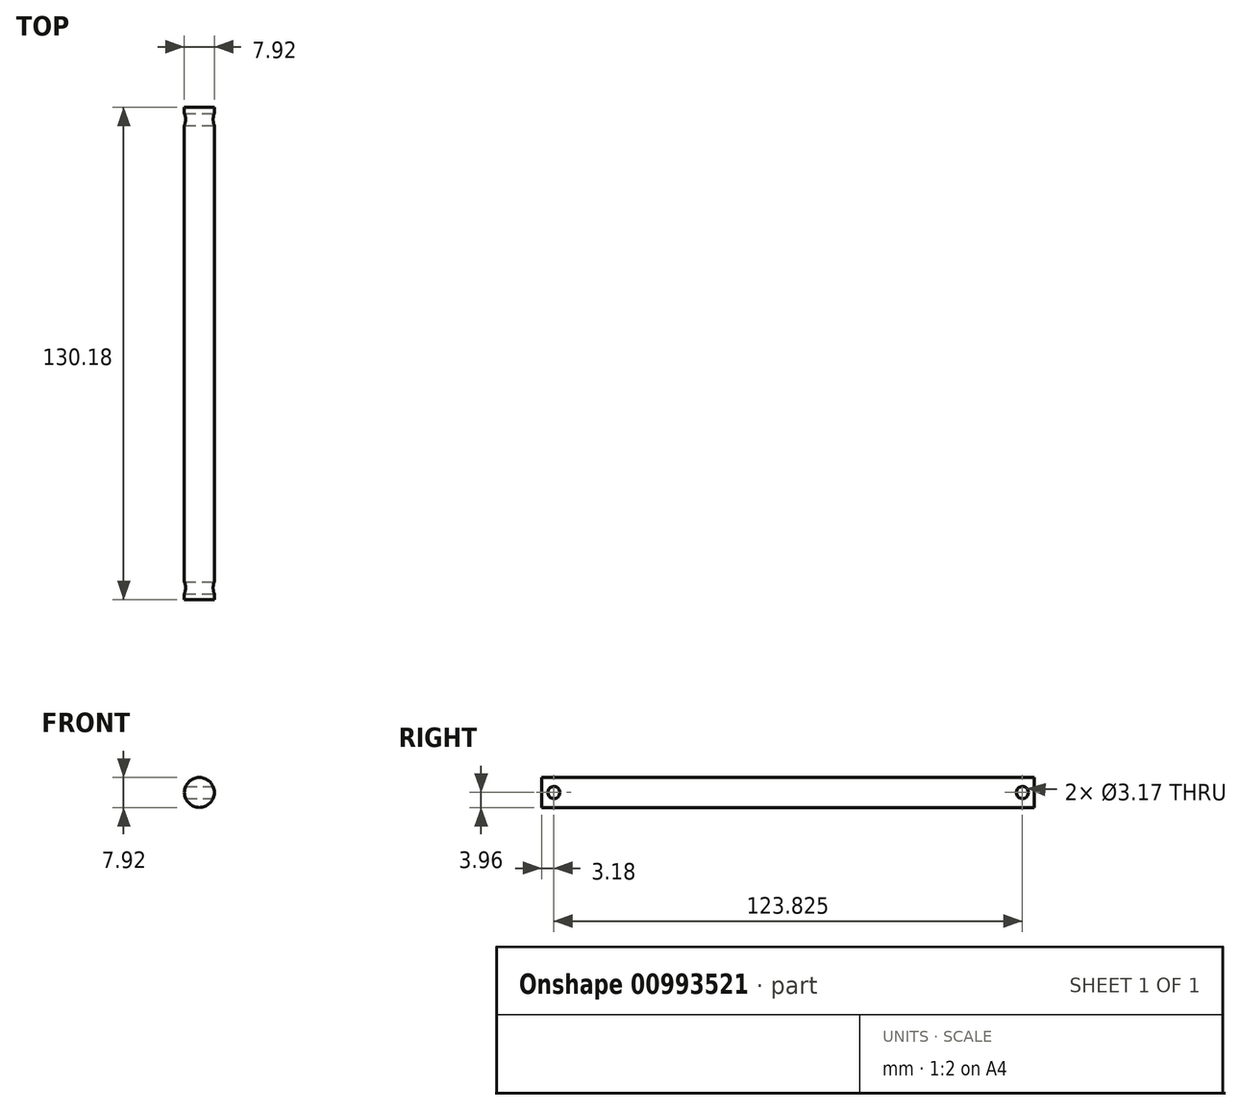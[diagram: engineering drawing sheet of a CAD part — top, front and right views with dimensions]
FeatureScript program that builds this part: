
annotation { "Feature Type Name" : "Feature", "Feature Type Description" : "" }
export const myFeature = defineFeature(function(context is Context, id is Id, definition is map)
    precondition{}
    {
        {
            var Q0;
            Q0=qCreatedBy(makeId("Front.planeOp"),FACE);
            var sketch = newSketch(context, id + "F0", { "sketchPlane" : qUnion([Q0])});
            skLineSegment(sketch, "E0.bottom", {"start": v(3.96, -3.96) * mm, "end": v(-3.96, -3.96) * mm});
            skLineSegment(sketch, "E0.top", {"start": v(3.96, 3.96) * mm, "end": v(-3.96, 3.96) * mm});
            skLineSegment(sketch, "E0.left", {"start": v(3.96, -3.96) * mm, "end": v(3.96, 3.96) * mm});
            skLineSegment(sketch, "E0.right", {"start": v(-3.96, -3.96) * mm, "end": v(-3.96, 3.96) * mm});
            skPoint(sketch, "E0.middle", {"position": v(0, 0) * mm});
            skSolve(sketch);
        }
        {
            var Q0;
            Q0=makeQuery(id+"F0.imprint","IMPRINT",FACE,{"disambiguationData":[TD([[makeQuery(id+"F0.imprint","IMPRINT",EDGE,{"derivedFrom":sQuery(id+"F0.wireOp",EDGE,"E0.bottom")}),-1.0]])]});
            extrude(context, id + "F1", {"entities" : qUnion([Q0]), "depth" : 130.17 * mm, "offsetDistance" : 25.4 * mm});
        }
        {
            var Q0;
            Q0=makeQuery(id+"F1.opExtrude","SWEPT_FACE",FACE,{"disambiguationData":[OSD([sQuery(id+"F0.wireOp",EDGE,"E0.left")])]});
            var sketch = newSketch(context, id + "F2", { "sketchPlane" : qUnion([Q0])});
            skLineSegment(sketch, "E1", {"start": v(0, 0) * mm, "end": v(-3.18, 0) * mm});
            skCircle(sketch, "E2", {"center": v(-3.18, 0) * mm, "radius": 1.59 * mm});
            skLineSegment(sketch, "E3", {"start": v(-130.18, 0) * mm, "end": v(-127, 0) * mm});
            skCircle(sketch, "E4", {"center": v(-127, 0) * mm, "radius": 1.59 * mm});
            skSolve(sketch);
        }
        {
            var Q0;
            Q0=makeQuery(id+"F2.imprint","IMPRINT",FACE,{"disambiguationData":[TD([[makeQuery(id+"F2.imprint","IMPRINT",EDGE,{"derivedFrom":sQuery(id+"F2.wireOp",EDGE,"E4")}),1.0]])]});
            var Q1;
            Q1=makeQuery(id+"F2.imprint","IMPRINT",FACE,{"disambiguationData":[TD([[makeQuery(id+"F2.imprint","IMPRINT",EDGE,{"derivedFrom":sQuery(id+"F2.wireOp",EDGE,"E2")}),1.0]])]});
            extrude(context, id + "F3", {"entities" : qUnion([Q0, Q1]), "operationType" : NewBodyOperationType.REMOVE, "oppositeDirection" : true, "depth" : 25.4 * mm, "offsetDistance" : 25.4 * mm});
        }
        {
            var Q0;
            Q0=makeQuery(id+"F1.opExtrude","CAP_FACE",FACE,{"disambiguationData":[OSD([sQuery(id+"F0.wireOp",EDGE,"E0.bottom"),sQuery(id+"F0.wireOp",EDGE,"E0.top"),sQuery(id+"F0.wireOp",EDGE,"E0.left"),sQuery(id+"F0.wireOp",EDGE,"E0.right")])],"isStart":true});
            var sketch = newSketch(context, id + "F4", { "sketchPlane" : qUnion([Q0])});
            skCircle(sketch, "E5", {"center": v(0, 0) * mm, "radius": 3.96 * mm});
            skSolve(sketch);
        }
        {
            var Q0;
            {var subQ0=sQuery(id+"F4.wireOp",EDGE,"E5");var subQ1=makeQuery(id+"F1.opExtrude","CAP_EDGE",EDGE,{"disambiguationData":[OSD([sQuery(id+"F0.wireOp",EDGE,"E0.top")])],"isStart":true});var subQ2=makeQuery(id+"F4.imprint","INTERSECT",VERTEX,{"derivedFrom":[subQ1,subQ0]});Q0=makeQuery(id+"F4.imprint","IMPRINT",FACE,{"disambiguationData":[TD([[makeQuery(id+"F4.imprint","IMPRINT",EDGE,{"disambiguationData":[TD([[subQ2,-1.0]])],"derivedFrom":subQ0}),-1.0]])]});}
            var Q1;
            {var subQ0=sQuery(id+"F4.wireOp",EDGE,"E5");var subQ1=makeQuery(id+"F1.opExtrude","CAP_EDGE",EDGE,{"disambiguationData":[OSD([sQuery(id+"F0.wireOp",EDGE,"E0.top")])],"isStart":true});var subQ2=makeQuery(id+"F4.imprint","INTERSECT",VERTEX,{"derivedFrom":[subQ1,subQ0]});Q1=makeQuery(id+"F4.imprint","IMPRINT",FACE,{"disambiguationData":[TD([[makeQuery(id+"F4.imprint","IMPRINT",EDGE,{"disambiguationData":[TD([[subQ2,1.0]])],"derivedFrom":subQ0}),-1.0]])]});}
            var Q2;
            {var subQ0=sQuery(id+"F4.wireOp",EDGE,"E5");var subQ1=makeQuery(id+"F1.opExtrude","CAP_EDGE",EDGE,{"disambiguationData":[OSD([sQuery(id+"F0.wireOp",EDGE,"E0.right")])],"isStart":true});var subQ2=makeQuery(id+"F4.imprint","INTERSECT",VERTEX,{"derivedFrom":[subQ1,subQ0]});Q2=makeQuery(id+"F4.imprint","IMPRINT",FACE,{"disambiguationData":[TD([[makeQuery(id+"F4.imprint","IMPRINT",EDGE,{"disambiguationData":[TD([[subQ2,1.0]])],"derivedFrom":subQ0}),-1.0]])]});}
            var Q3;
            {var subQ0=sQuery(id+"F4.wireOp",EDGE,"E5");var subQ1=makeQuery(id+"F1.opExtrude","CAP_EDGE",EDGE,{"disambiguationData":[OSD([sQuery(id+"F0.wireOp",EDGE,"E0.left")])],"isStart":true});var subQ2=makeQuery(id+"F4.imprint","INTERSECT",VERTEX,{"derivedFrom":[subQ1,subQ0]});Q3=makeQuery(id+"F4.imprint","IMPRINT",FACE,{"disambiguationData":[TD([[makeQuery(id+"F4.imprint","IMPRINT",EDGE,{"disambiguationData":[TD([[subQ2,-1.0]])],"derivedFrom":subQ0}),-1.0]])]});}
            extrude(context, id + "F5", {"entities" : qUnion([Q0, Q1, Q2, Q3]), "operationType" : NewBodyOperationType.REMOVE, "oppositeDirection" : true, "depth" : 508 * mm, "offsetDistance" : 25.4 * mm});
        }
    });
